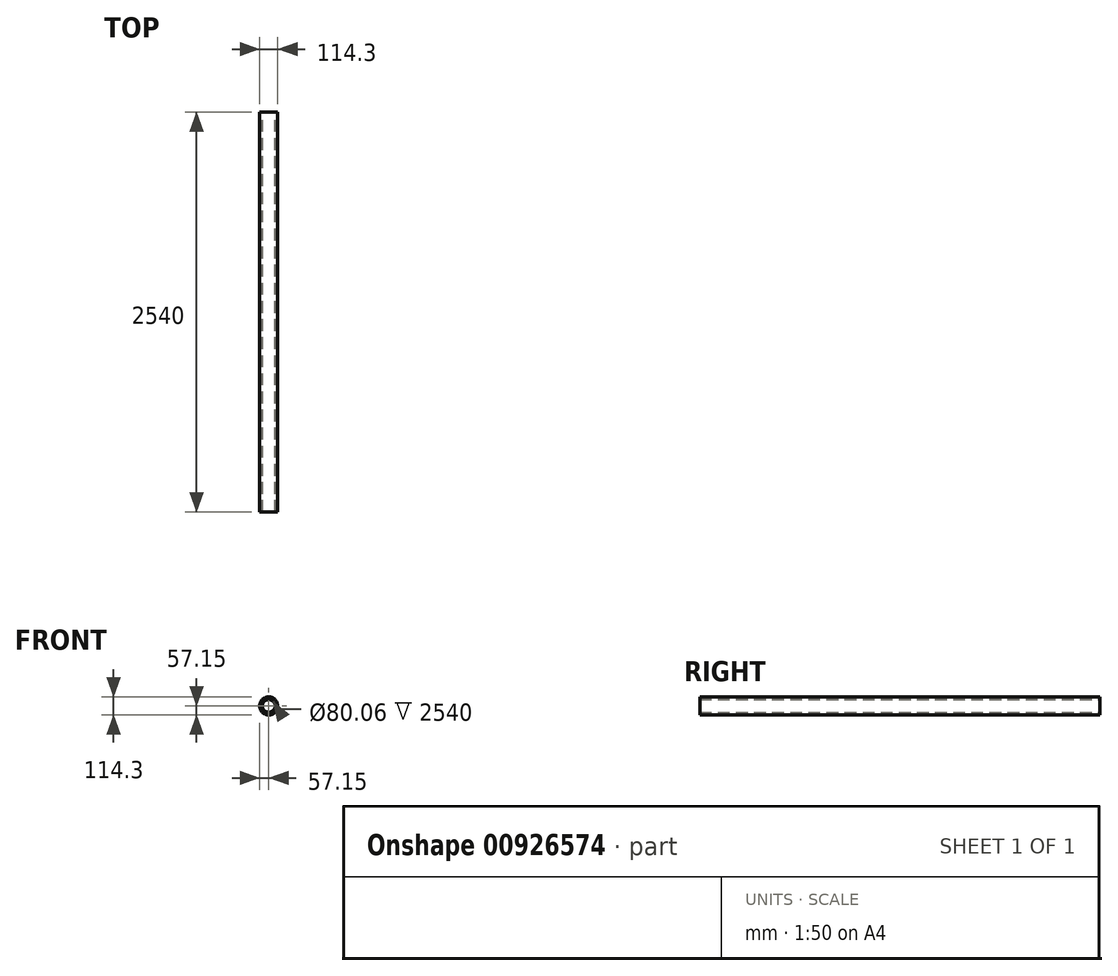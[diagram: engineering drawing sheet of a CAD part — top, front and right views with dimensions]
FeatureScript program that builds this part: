
annotation { "Feature Type Name" : "Feature", "Feature Type Description" : "" }
export const myFeature = defineFeature(function(context is Context, id is Id, definition is map)
    precondition{}
    {
        {
            var Q0;
            Q0=qCreatedBy(makeId("Front.planeOp"),FACE);
            var sketch = newSketch(context, id + "F0", { "sketchPlane" : qUnion([Q0])});
            skCircle(sketch, "E0", {"center": v(0, 0) * mm, "radius": 40.03 * mm});
            skCircle(sketch, "E1", {"center": v(0, 0) * mm, "radius": 57.15 * mm});
            skSolve(sketch);
        }
        {
            var Q0;
            Q0=makeQuery(id+"F0.imprint","IMPRINT",FACE,{"disambiguationData":[TD([[makeQuery(id+"F0.imprint","IMPRINT",EDGE,{"derivedFrom":sQuery(id+"F0.wireOp",EDGE,"E0")}),-1.0]])]});
            extrude(context, id + "F1", {"entities" : qUnion([Q0]), "depth" : 2540 * mm, "offsetDistance" : 25.4 * mm});
        }
    });
